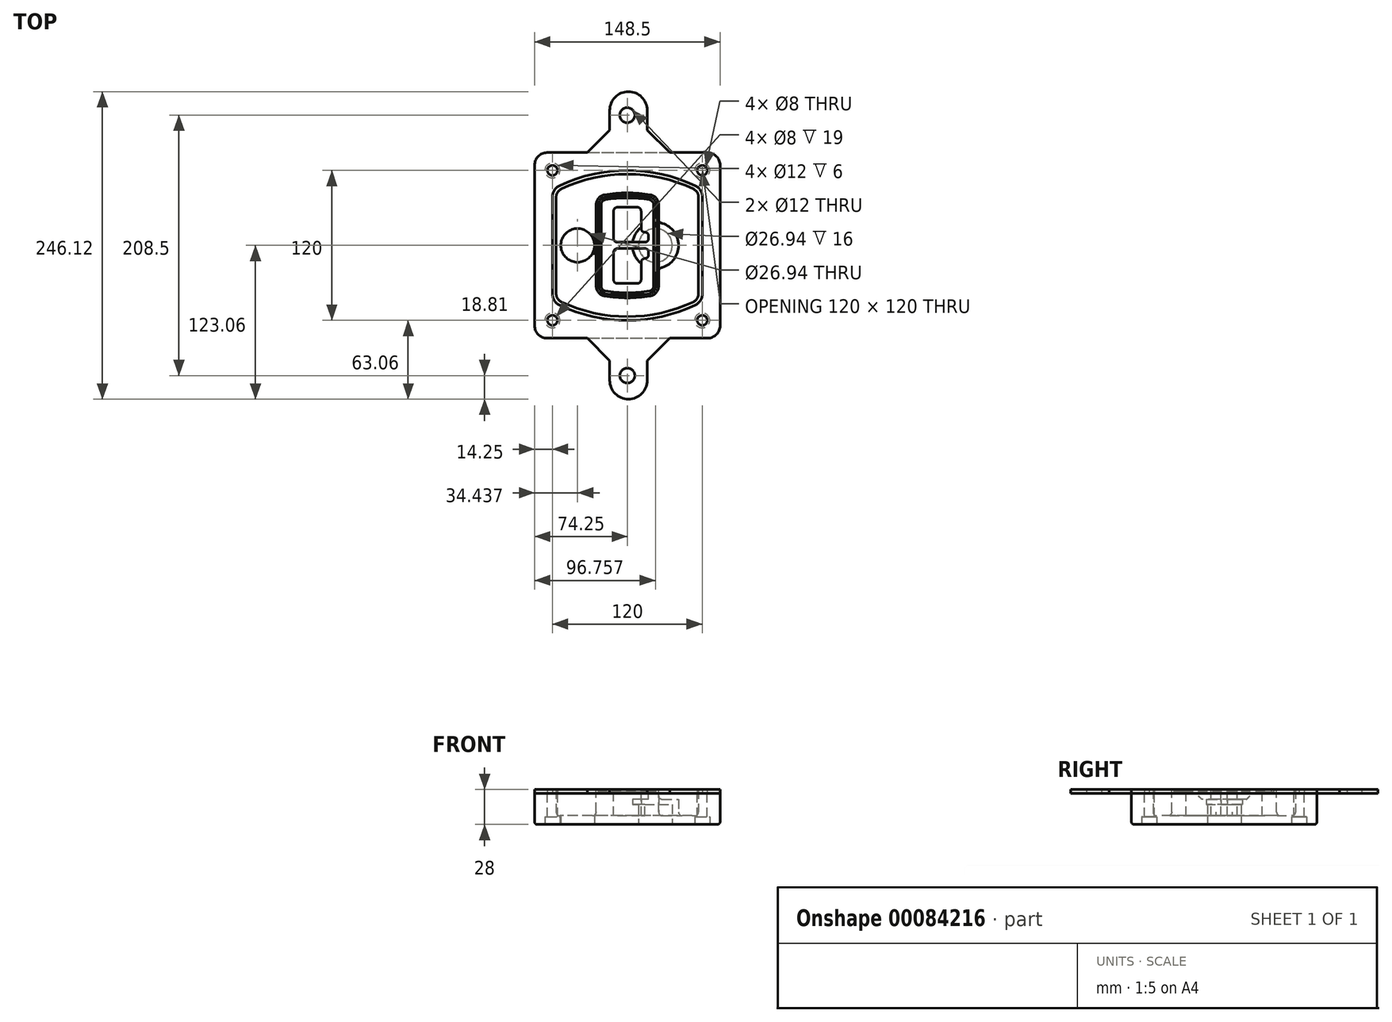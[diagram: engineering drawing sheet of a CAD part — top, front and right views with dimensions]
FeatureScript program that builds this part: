
annotation { "Feature Type Name" : "Feature", "Feature Type Description" : "" }
export const myFeature = defineFeature(function(context is Context, id is Id, definition is map)
    precondition{}
    {
        {
            var Q0;
            Q0=qCreatedBy(makeId("Top.planeOp"),FACE);
            var sketch = newSketch(context, id + "F0", { "sketchPlane" : qUnion([Q0])});
            skPoint(sketch, "E0.rect.middle", {"position": v(0, 0) * mm});
            skLineSegment(sketch, "E1.bottom", {"start": v(-64.25, -74.25) * mm, "end": v(64.25, -74.25) * mm});
            skLineSegment(sketch, "E1.top", {"start": v(-64.25, 74.25) * mm, "end": v(64.25, 74.25) * mm});
            skLineSegment(sketch, "E1.left", {"start": v(-74.25, -64.25) * mm, "end": v(-74.25, 64.25) * mm});
            skLineSegment(sketch, "E1.right", {"start": v(74.25, -64.25) * mm, "end": v(74.25, 64.25) * mm});
            skLineSegment(sketch, "E2", {"start": v(-74.25, 74.25) * mm, "end": v(74.25, -74.25) * mm, "construction": true});
            skLineSegment(sketch, "E3", {"start": v(74.25, 74.25) * mm, "end": v(-74.25, -74.25) * mm, "construction": true});
            skCircle(sketch, "E4", {"center": v(-60, 60) * mm, "radius": 4 * mm});
            skCircle(sketch, "E5", {"center": v(60, 60) * mm, "radius": 4 * mm});
            skCircle(sketch, "E6", {"center": v(60, -60) * mm, "radius": 4 * mm});
            skCircle(sketch, "E7", {"center": v(-60, -60) * mm, "radius": 4 * mm});
            skLineSegment(sketch, "E8", {"start": v(-60, 60) * mm, "end": v(60, 60) * mm, "construction": true});
            skLineSegment(sketch, "E9", {"start": v(60, 60) * mm, "end": v(60, -60) * mm, "construction": true});
            skLineSegment(sketch, "E10", {"start": v(60, -60) * mm, "end": v(-60, -60) * mm, "construction": true});
            skLineSegment(sketch, "E11", {"start": v(-60, -60) * mm, "end": v(-60, 60) * mm, "construction": true});
            skLineSegment(sketch, "E12", {"start": v(-60, 38.83) * mm, "end": v(-60, -38.83) * mm});
            skLineSegment(sketch, "E13", {"start": v(60, 38.83) * mm, "end": v(60, -38.83) * mm});
            skArc(sketch, "E14", {"start": v(54.26, 47.88) * mm, "mid": v(0, 60) * mm, "end": v(-54.26, 47.88) * mm});
            skArc(sketch, "E15", {"start": v(-54.26, -47.88) * mm, "mid": v(0, -60) * mm, "end": v(54.26, -47.88) * mm});
            skLineSegment(sketch, "E16", {"start": v(-60, 0) * mm, "end": v(60, 0) * mm, "construction": true});
            skPoint(sketch, "E17.visualSharp", {"position": v(-60, -45) * mm});
            skArc(sketch, "E17.filletArc", {"start": v(-60, -38.83) * mm, "mid": v(-58.44, -44.2) * mm, "end": v(-54.26, -47.88) * mm});
            skPoint(sketch, "E18.visualSharp", {"position": v(-60, 45) * mm});
            skArc(sketch, "E18.filletArc", {"start": v(-54.26, 47.88) * mm, "mid": v(-58.44, 44.2) * mm, "end": v(-60, 38.83) * mm});
            skPoint(sketch, "E19.visualSharp", {"position": v(60, 45) * mm});
            skArc(sketch, "E19.filletArc", {"start": v(60, 38.83) * mm, "mid": v(58.44, 44.2) * mm, "end": v(54.26, 47.88) * mm});
            skPoint(sketch, "E20.visualSharp", {"position": v(60, -45) * mm});
            skArc(sketch, "E20.filletArc", {"start": v(54.26, -47.88) * mm, "mid": v(58.44, -44.2) * mm, "end": v(60, -38.83) * mm});
            skPoint(sketch, "E21.visualSharp", {"position": v(-74.25, 74.25) * mm});
            skArc(sketch, "E21.filletArc", {"start": v(-64.25, 74.25) * mm, "mid": v(-71.32, 71.32) * mm, "end": v(-74.25, 64.25) * mm});
            skPoint(sketch, "E22.visualSharp", {"position": v(74.25, 74.25) * mm});
            skArc(sketch, "E22.filletArc", {"start": v(74.25, 64.25) * mm, "mid": v(71.32, 71.32) * mm, "end": v(64.25, 74.25) * mm});
            skPoint(sketch, "E23.visualSharp", {"position": v(74.25, -74.25) * mm});
            skArc(sketch, "E23.filletArc", {"start": v(64.25, -74.25) * mm, "mid": v(71.32, -71.32) * mm, "end": v(74.25, -64.25) * mm});
            skPoint(sketch, "E24.visualSharp", {"position": v(-74.25, -74.25) * mm});
            skArc(sketch, "E24.filletArc", {"start": v(-74.25, -64.25) * mm, "mid": v(-71.32, -71.32) * mm, "end": v(-64.25, -74.25) * mm});
            skArc(sketch, "E25.0", {"start": v(57, 38.83) * mm, "mid": v(55.9, 42.58) * mm, "end": v(52.98, 45.17) * mm});
            skLineSegment(sketch, "E25.1", {"start": v(57, 38.83) * mm, "end": v(57, -38.83) * mm});
            skArc(sketch, "E25.2", {"start": v(52.98, -45.17) * mm, "mid": v(55.9, -42.58) * mm, "end": v(57, -38.83) * mm});
            skArc(sketch, "E25.3", {"start": v(-52.98, -45.17) * mm, "mid": v(0, -57) * mm, "end": v(52.98, -45.17) * mm});
            skArc(sketch, "E25.4", {"start": v(-57, -38.83) * mm, "mid": v(-55.9, -42.58) * mm, "end": v(-52.98, -45.17) * mm});
            skArc(sketch, "E25.5", {"start": v(52.98, 45.17) * mm, "mid": v(0, 57) * mm, "end": v(-52.98, 45.17) * mm});
            skLineSegment(sketch, "E25.6", {"start": v(-57, 38.83) * mm, "end": v(-57, -38.83) * mm});
            skArc(sketch, "E25.7", {"start": v(-52.98, 45.17) * mm, "mid": v(-55.9, 42.58) * mm, "end": v(-57, 38.83) * mm});
            skArc(sketch, "E26.0", {"start": v(-55.96, 51.5) * mm, "mid": v(-61.82, 46.33) * mm, "end": v(-64, 38.83) * mm});
            skArc(sketch, "E26.1", {"start": v(55.96, 51.5) * mm, "mid": v(0, 64) * mm, "end": v(-55.96, 51.5) * mm});
            skArc(sketch, "E26.2", {"start": v(64, 38.83) * mm, "mid": v(61.82, 46.33) * mm, "end": v(55.96, 51.5) * mm});
            skLineSegment(sketch, "E26.3", {"start": v(64, 38.83) * mm, "end": v(64, -38.83) * mm});
            skArc(sketch, "E26.4", {"start": v(55.96, -51.5) * mm, "mid": v(61.82, -46.33) * mm, "end": v(64, -38.83) * mm});
            skLineSegment(sketch, "E26.5", {"start": v(-64, 38.83) * mm, "end": v(-64, -38.83) * mm});
            skArc(sketch, "E26.6", {"start": v(-55.96, -51.5) * mm, "mid": v(0, -64) * mm, "end": v(55.96, -51.5) * mm});
            skArc(sketch, "E26.7", {"start": v(-64, -38.83) * mm, "mid": v(-61.82, -46.33) * mm, "end": v(-55.96, -51.5) * mm});
            skSolve(sketch);
        }
        {
            var Q0;
            Q0=makeQuery(id+"F0.imprint","IMPRINT",FACE,{"disambiguationData":[TD([[makeQuery(id+"F0.imprint","IMPRINT",EDGE,{"derivedFrom":sQuery(id+"F0.wireOp",EDGE,"E1.bottom")}),1.0]])]});
            var Q1;
            Q1=makeQuery(id+"F0.imprint","IMPRINT",FACE,{"disambiguationData":[TD([[makeQuery(id+"F0.imprint","IMPRINT",EDGE,{"derivedFrom":sQuery(id+"F0.wireOp",EDGE,"E12")}),1.0]])]});
            var Q2;
            Q2=makeQuery(id+"F0.imprint","IMPRINT",FACE,{"disambiguationData":[TD([[makeQuery(id+"F0.imprint","IMPRINT",EDGE,{"derivedFrom":sQuery(id+"F0.wireOp",EDGE,"E25.0")}),1.0]])]});
            var Q3;
            Q3=makeQuery(id+"F0.imprint","IMPRINT",FACE,{"disambiguationData":[TD([[makeQuery(id+"F0.imprint","IMPRINT",EDGE,{"derivedFrom":sQuery(id+"F0.wireOp",EDGE,"E12")}),-1.0]])]});
            extrude(context, id + "F1", {"entities" : qUnion([Q0, Q1, Q2, Q3]), "oppositeDirection" : true, "depth" : 25 * mm});
        }
        {
            var Q0;
            Q0=makeQuery(id+"F0.imprint","IMPRINT",FACE,{"disambiguationData":[TD([[makeQuery(id+"F0.imprint","IMPRINT",EDGE,{"derivedFrom":sQuery(id+"F0.wireOp",EDGE,"E12")}),1.0]])]});
            extrude(context, id + "F2", {"entities" : qUnion([Q0]), "operationType" : NewBodyOperationType.ADD, "depth" : 3 * mm});
        }
        {
            var Q0;
            Q0=makeQuery(id+"F0.imprint","IMPRINT",FACE,{"disambiguationData":[TD([[makeQuery(id+"F0.imprint","IMPRINT",EDGE,{"derivedFrom":sQuery(id+"F0.wireOp",EDGE,"E25.0")}),1.0]])]});
            extrude(context, id + "F3", {"entities" : qUnion([Q0]), "operationType" : NewBodyOperationType.REMOVE, "oppositeDirection" : true, "depth" : 18 * mm});
        }
        {
            var Q0;
            Q0=makeQuery(id+"F2.opExtrude","CAP_FACE",FACE,{"disambiguationData":[OSD([sQuery(id+"F0.wireOp",EDGE,"E12"),sQuery(id+"F0.wireOp",EDGE,"E13"),sQuery(id+"F0.wireOp",EDGE,"E14"),sQuery(id+"F0.wireOp",EDGE,"E15"),sQuery(id+"F0.wireOp",EDGE,"E17.filletArc"),sQuery(id+"F0.wireOp",EDGE,"E18.filletArc"),sQuery(id+"F0.wireOp",EDGE,"E19.filletArc"),sQuery(id+"F0.wireOp",EDGE,"E20.filletArc"),sQuery(id+"F0.wireOp",EDGE,"E25.0"),sQuery(id+"F0.wireOp",EDGE,"E25.1"),sQuery(id+"F0.wireOp",EDGE,"E25.2"),sQuery(id+"F0.wireOp",EDGE,"E25.3"),sQuery(id+"F0.wireOp",EDGE,"E25.4"),sQuery(id+"F0.wireOp",EDGE,"E25.5"),sQuery(id+"F0.wireOp",EDGE,"E25.6"),sQuery(id+"F0.wireOp",EDGE,"E25.7")])],"isStart":false});
            var sketch = newSketch(context, id + "F4", { "sketchPlane" : qUnion([Q0])});
            skArc(sketch, "E27.0", {"start": v(-18.34, -40.45) * mm, "mid": v(0, -42) * mm, "end": v(18.34, -40.45) * mm});
            skArc(sketch, "E28.0", {"start": v(18.34, 40.45) * mm, "mid": v(0, 42) * mm, "end": v(-18.34, 40.45) * mm});
            skLineSegment(sketch, "E29", {"start": v(-25, 32.57) * mm, "end": v(-25, -32.57) * mm});
            skLineSegment(sketch, "E30", {"start": v(25, 32.57) * mm, "end": v(25, -32.57) * mm});
            skLineSegment(sketch, "E31", {"start": v(-25, 39.1) * mm, "end": v(25, 39.1) * mm, "construction": true});
            skLineSegment(sketch, "E32", {"start": v(-25, -39.1) * mm, "end": v(25, -39.1) * mm, "construction": true});
            skPoint(sketch, "E33.visualSharp", {"position": v(-25, 39.1) * mm});
            skArc(sketch, "E33.filletArc", {"start": v(-18.34, 40.45) * mm, "mid": v(-23.11, 37.73) * mm, "end": v(-25, 32.57) * mm});
            skPoint(sketch, "E34.visualSharp", {"position": v(25, 39.1) * mm});
            skArc(sketch, "E34.filletArc", {"start": v(25, 32.57) * mm, "mid": v(23.11, 37.73) * mm, "end": v(18.34, 40.45) * mm});
            skPoint(sketch, "E35.visualSharp", {"position": v(25, -39.1) * mm});
            skArc(sketch, "E35.filletArc", {"start": v(18.34, -40.45) * mm, "mid": v(23.11, -37.73) * mm, "end": v(25, -32.57) * mm});
            skPoint(sketch, "E36.visualSharp", {"position": v(-25, -39.1) * mm});
            skArc(sketch, "E36.filletArc", {"start": v(-25, -32.57) * mm, "mid": v(-23.11, -37.73) * mm, "end": v(-18.34, -40.45) * mm});
            skArc(sketch, "E37.0", {"start": v(52.98, 45.17) * mm, "mid": v(0, 57) * mm, "end": v(-52.98, 45.17) * mm});
            skArc(sketch, "E37.1", {"start": v(-52.98, 45.17) * mm, "mid": v(-55.9, 42.58) * mm, "end": v(-57, 38.83) * mm});
            skLineSegment(sketch, "E37.2", {"start": v(-57, 38.83) * mm, "end": v(-57, -38.83) * mm});
            skArc(sketch, "E37.3", {"start": v(-57, -38.83) * mm, "mid": v(-55.9, -42.58) * mm, "end": v(-52.98, -45.17) * mm});
            skArc(sketch, "E37.4", {"start": v(-52.98, -45.17) * mm, "mid": v(0, -57) * mm, "end": v(52.98, -45.17) * mm});
            skArc(sketch, "E37.5", {"start": v(52.98, -45.17) * mm, "mid": v(55.9, -42.58) * mm, "end": v(57, -38.83) * mm});
            skLineSegment(sketch, "E37.6", {"start": v(57, 38.83) * mm, "end": v(57, -38.83) * mm});
            skArc(sketch, "E37.7", {"start": v(57, 38.83) * mm, "mid": v(55.9, 42.58) * mm, "end": v(52.98, 45.17) * mm});
            skLineSegment(sketch, "E38.0", {"start": v(23, 32.57) * mm, "end": v(23, -32.57) * mm});
            skArc(sketch, "E38.1", {"start": v(18, -38.48) * mm, "mid": v(21.58, -36.44) * mm, "end": v(23, -32.57) * mm});
            skArc(sketch, "E38.2", {"start": v(-18, -38.48) * mm, "mid": v(0, -40) * mm, "end": v(18, -38.48) * mm});
            skArc(sketch, "E38.3", {"start": v(-23, -32.57) * mm, "mid": v(-21.58, -36.44) * mm, "end": v(-18, -38.48) * mm});
            skLineSegment(sketch, "E38.4", {"start": v(-23, 32.57) * mm, "end": v(-23, -32.57) * mm});
            skArc(sketch, "E38.5", {"start": v(23, 32.57) * mm, "mid": v(21.58, 36.44) * mm, "end": v(18, 38.48) * mm});
            skArc(sketch, "E38.6", {"start": v(-18, 38.48) * mm, "mid": v(-21.58, 36.44) * mm, "end": v(-23, 32.57) * mm});
            skArc(sketch, "E38.7", {"start": v(18, 38.48) * mm, "mid": v(0, 40) * mm, "end": v(-18, 38.48) * mm});
            skArc(sketch, "E39.0", {"start": v(21, 32.57) * mm, "mid": v(20.06, 35.15) * mm, "end": v(17.67, 36.5) * mm});
            skLineSegment(sketch, "E39.1", {"start": v(21, 32.57) * mm, "end": v(21, -32.57) * mm});
            skArc(sketch, "E39.2", {"start": v(17.67, -36.5) * mm, "mid": v(20.06, -35.15) * mm, "end": v(21, -32.57) * mm});
            skArc(sketch, "E39.3", {"start": v(-17.67, -36.5) * mm, "mid": v(0, -38) * mm, "end": v(17.67, -36.5) * mm});
            skArc(sketch, "E39.4", {"start": v(-21, -32.57) * mm, "mid": v(-20.06, -35.15) * mm, "end": v(-17.67, -36.5) * mm});
            skArc(sketch, "E39.5", {"start": v(17.67, 36.5) * mm, "mid": v(0, 38) * mm, "end": v(-17.67, 36.5) * mm});
            skLineSegment(sketch, "E39.6", {"start": v(-21, 32.57) * mm, "end": v(-21, -32.57) * mm});
            skArc(sketch, "E39.7", {"start": v(-17.67, 36.5) * mm, "mid": v(-20.06, 35.15) * mm, "end": v(-21, 32.57) * mm});
            skLineSegment(sketch, "E40", {"start": v(-25, 0) * mm, "end": v(25, 0) * mm, "construction": true});
            skLineSegment(sketch, "E41", {"start": v(-11, 5.5) * mm, "end": v(-11, 27.5) * mm});
            skLineSegment(sketch, "E42", {"start": v(-8, 30.5) * mm, "end": v(8, 30.5) * mm});
            skLineSegment(sketch, "E43", {"start": v(11, 27.5) * mm, "end": v(11, 13.5) * mm});
            skLineSegment(sketch, "E44", {"start": v(14, 10.5) * mm, "end": v(14, 10.5) * mm});
            skLineSegment(sketch, "E45", {"start": v(17, 7.5) * mm, "end": v(17, 5.5) * mm});
            skLineSegment(sketch, "E46", {"start": v(14, 2.5) * mm, "end": v(-8, 2.5) * mm});
            skPoint(sketch, "E47.visualSharp", {"position": v(-11, 30.5) * mm});
            skArc(sketch, "E47.filletArc", {"start": v(-8, 30.5) * mm, "mid": v(-10.12, 29.62) * mm, "end": v(-11, 27.5) * mm});
            skPoint(sketch, "E48.visualSharp", {"position": v(11, 30.5) * mm});
            skArc(sketch, "E48.filletArc", {"start": v(11, 27.5) * mm, "mid": v(10.12, 29.62) * mm, "end": v(8, 30.5) * mm});
            skPoint(sketch, "E49.visualSharp", {"position": v(11, 10.5) * mm});
            skArc(sketch, "E49.filletArc", {"start": v(11, 13.5) * mm, "mid": v(11.88, 11.38) * mm, "end": v(14, 10.5) * mm});
            skPoint(sketch, "E50.visualSharp", {"position": v(17, 10.5) * mm});
            skArc(sketch, "E50.filletArc", {"start": v(17, 7.5) * mm, "mid": v(16.12, 9.62) * mm, "end": v(14, 10.5) * mm});
            skPoint(sketch, "E51.visualSharp", {"position": v(17, 2.5) * mm});
            skArc(sketch, "E51.filletArc", {"start": v(14, 2.5) * mm, "mid": v(16.12, 3.38) * mm, "end": v(17, 5.5) * mm});
            skPoint(sketch, "E52.visualSharp", {"position": v(-11, 2.5) * mm});
            skArc(sketch, "E52.filletArc", {"start": v(-11, 5.5) * mm, "mid": v(-10.12, 3.38) * mm, "end": v(-8, 2.5) * mm});
            skLineSegment(sketch, "E53.0.MirrorCS", {"start": v(14, -2.5) * mm, "end": v(-8, -2.5) * mm});
            skArc(sketch, "E54.0.MirrorCS", {"start": v(-11, -5.5) * mm, "mid": v(-10.12, -3.38) * mm, "end": v(-8, -2.5) * mm});
            skLineSegment(sketch, "E55.0.MirrorCS", {"start": v(-11, -5.5) * mm, "end": v(-11, -27.5) * mm});
            skArc(sketch, "E56.0.MirrorCS", {"start": v(-8, -30.5) * mm, "mid": v(-10.12, -29.62) * mm, "end": v(-11, -27.5) * mm});
            skLineSegment(sketch, "E57.0.MirrorCS", {"start": v(-8, -30.5) * mm, "end": v(8, -30.5) * mm});
            skArc(sketch, "E58.0.MirrorCS", {"start": v(11, -27.5) * mm, "mid": v(10.12, -29.62) * mm, "end": v(8, -30.5) * mm});
            skLineSegment(sketch, "E59.0.MirrorCS", {"start": v(11, -27.5) * mm, "end": v(11, -13.5) * mm});
            skArc(sketch, "E60.0.MirrorCS", {"start": v(11, -13.5) * mm, "mid": v(11.88, -11.38) * mm, "end": v(14, -10.5) * mm});
            skArc(sketch, "E61.0.MirrorCS", {"start": v(17, -7.5) * mm, "mid": v(16.12, -9.62) * mm, "end": v(14, -10.5) * mm});
            skLineSegment(sketch, "E62.0.MirrorCS", {"start": v(17, -7.5) * mm, "end": v(17, -5.5) * mm});
            skArc(sketch, "E63.0.MirrorCS", {"start": v(14, -2.5) * mm, "mid": v(16.12, -3.38) * mm, "end": v(17, -5.5) * mm});
            skSolve(sketch);
        }
        {
            var Q0;
            Q0=makeQuery(id+"F4.imprint","IMPRINT",FACE,{"disambiguationData":[TD([[makeQuery(id+"F4.imprint","IMPRINT",EDGE,{"derivedFrom":sQuery(id+"F4.wireOp",EDGE,"E27.0")}),1.0]])]});
            var Q1;
            Q1=makeQuery(id+"F4.imprint","IMPRINT",FACE,{"disambiguationData":[TD([[makeQuery(id+"F4.imprint","IMPRINT",EDGE,{"derivedFrom":sQuery(id+"F4.wireOp",EDGE,"E38.0")}),-1.0]])]});
            var Q2;
            Q2=makeQuery(id+"F4.imprint","IMPRINT",FACE,{"disambiguationData":[TD([[makeQuery(id+"F4.imprint","IMPRINT",EDGE,{"derivedFrom":sQuery(id+"F4.wireOp",EDGE,"E39.0")}),1.0]])]});
            extrude(context, id + "F5", {"entities" : qUnion([Q0, Q1, Q2]), "operationType" : NewBodyOperationType.ADD, "endBound" : BoundingType.UP_TO_NEXT, "oppositeDirection" : true, "depth" : 25 * mm});
        }
        {
            var Q0;
            Q0=makeQuery(id+"F4.imprint","IMPRINT",FACE,{"disambiguationData":[TD([[makeQuery(id+"F4.imprint","IMPRINT",EDGE,{"derivedFrom":sQuery(id+"F4.wireOp",EDGE,"E38.0")}),-1.0]])]});
            extrude(context, id + "F6", {"entities" : qUnion([Q0]), "operationType" : NewBodyOperationType.REMOVE, "oppositeDirection" : true, "depth" : 2 * mm});
        }
        {
            var Q0;
            Q0=makeQuery(id+"F1.opExtrude","CAP_FACE",FACE,{"disambiguationData":[OSD([sQuery(id+"F0.wireOp",EDGE,"E1.bottom"),sQuery(id+"F0.wireOp",EDGE,"E1.top"),sQuery(id+"F0.wireOp",EDGE,"E1.left"),sQuery(id+"F0.wireOp",EDGE,"E1.right"),sQuery(id+"F0.wireOp",EDGE,"E4"),sQuery(id+"F0.wireOp",EDGE,"E5"),sQuery(id+"F0.wireOp",EDGE,"E6"),sQuery(id+"F0.wireOp",EDGE,"E7"),sQuery(id+"F0.wireOp",EDGE,"E21.filletArc"),sQuery(id+"F0.wireOp",EDGE,"E22.filletArc"),sQuery(id+"F0.wireOp",EDGE,"E23.filletArc"),sQuery(id+"F0.wireOp",EDGE,"E24.filletArc")])],"isStart":false});
            var sketch = newSketch(context, id + "F7", { "sketchPlane" : qUnion([Q0])});
            skCircle(sketch, "E64", {"center": v(22.5, 0) * mm, "radius": 13.47 * mm});
            skCircle(sketch, "E65", {"center": v(-39.81, 0) * mm, "radius": 13.47 * mm});
            skLineSegment(sketch, "E66", {"start": v(74.25, 0) * mm, "end": v(-74.25, 0) * mm});
            skCircle(sketch, "E67", {"center": v(22.5, 0) * mm, "radius": 18.47 * mm});
            skCircle(sketch, "E68", {"center": v(60, -60) * mm, "radius": 6 * mm});
            skCircle(sketch, "E69", {"center": v(-60, -60) * mm, "radius": 6 * mm});
            skCircle(sketch, "E70", {"center": v(-60, 60) * mm, "radius": 6 * mm});
            skCircle(sketch, "E71", {"center": v(60, 60) * mm, "radius": 6 * mm});
            skSolve(sketch);
        }
        {
            var Q0;
            {var subQ1=sQuery(id+"F7.wireOp",EDGE,"E66");var subQ4=sQuery(id+"F7.wireOp",EDGE,"E64");var subQ6=makeQuery(id+"F7.imprint","INTERSECT",VERTEX,{"disambiguationData":[OD(0.0)],"derivedFrom":[subQ4,subQ1]});Q0=makeQuery(id+"F7.imprint","IMPRINT",FACE,{"disambiguationData":[TD([[makeQuery(id+"F7.imprint","IMPRINT",EDGE,{"disambiguationData":[TD([[subQ6,-1.0]])],"derivedFrom":subQ4}),-1.0]])]});}
            var Q1;
            {var subQ0=sQuery(id+"F7.wireOp",EDGE,"E66");var subQ1=sQuery(id+"F7.wireOp",EDGE,"E64");var subQ3=makeQuery(id+"F7.imprint","INTERSECT",VERTEX,{"disambiguationData":[OD(0.0)],"derivedFrom":[subQ1,subQ0]});Q1=makeQuery(id+"F7.imprint","IMPRINT",FACE,{"disambiguationData":[TD([[makeQuery(id+"F7.imprint","IMPRINT",EDGE,{"disambiguationData":[TD([[subQ3,-1.0]])],"derivedFrom":subQ1}),1.0]])]});}
            var Q2;
            {var subQ0=sQuery(id+"F7.wireOp",EDGE,"E66");var subQ1=sQuery(id+"F7.wireOp",EDGE,"E64");var subQ3=makeQuery(id+"F7.imprint","INTERSECT",VERTEX,{"disambiguationData":[OD(0.0)],"derivedFrom":[subQ1,subQ0]});Q2=makeQuery(id+"F7.imprint","IMPRINT",FACE,{"disambiguationData":[TD([[makeQuery(id+"F7.imprint","IMPRINT",EDGE,{"disambiguationData":[TD([[subQ3,1.0]])],"derivedFrom":subQ1}),1.0]])]});}
            var Q3;
            {var subQ1=sQuery(id+"F7.wireOp",EDGE,"E66");var subQ4=sQuery(id+"F7.wireOp",EDGE,"E64");var subQ6=makeQuery(id+"F7.imprint","INTERSECT",VERTEX,{"disambiguationData":[OD(0.0)],"derivedFrom":[subQ4,subQ1]});Q3=makeQuery(id+"F7.imprint","IMPRINT",FACE,{"disambiguationData":[TD([[makeQuery(id+"F7.imprint","IMPRINT",EDGE,{"disambiguationData":[TD([[subQ6,1.0]])],"derivedFrom":subQ4}),-1.0]])]});}
            extrude(context, id + "F8", {"entities" : qUnion([Q0, Q1, Q2, Q3]), "operationType" : NewBodyOperationType.ADD, "oppositeDirection" : true, "depth" : 20 * mm});
        }
        {
            var Q0;
            {var subQ0=sQuery(id+"F7.wireOp",EDGE,"E66");var subQ1=sQuery(id+"F7.wireOp",EDGE,"E64");var subQ3=makeQuery(id+"F7.imprint","INTERSECT",VERTEX,{"disambiguationData":[OD(0.0)],"derivedFrom":[subQ1,subQ0]});Q0=makeQuery(id+"F7.imprint","IMPRINT",FACE,{"disambiguationData":[TD([[makeQuery(id+"F7.imprint","IMPRINT",EDGE,{"disambiguationData":[TD([[subQ3,-1.0]])],"derivedFrom":subQ1}),1.0]])]});}
            var Q1;
            {var subQ0=sQuery(id+"F7.wireOp",EDGE,"E66");var subQ1=sQuery(id+"F7.wireOp",EDGE,"E64");var subQ3=makeQuery(id+"F7.imprint","INTERSECT",VERTEX,{"disambiguationData":[OD(0.0)],"derivedFrom":[subQ1,subQ0]});Q1=makeQuery(id+"F7.imprint","IMPRINT",FACE,{"disambiguationData":[TD([[makeQuery(id+"F7.imprint","IMPRINT",EDGE,{"disambiguationData":[TD([[subQ3,1.0]])],"derivedFrom":subQ1}),1.0]])]});}
            extrude(context, id + "F9", {"entities" : qUnion([Q0, Q1]), "operationType" : NewBodyOperationType.REMOVE, "oppositeDirection" : true, "depth" : 16 * mm});
        }
        {
            var Q0;
            {var subQ0=sQuery(id+"F7.wireOp",EDGE,"E66");var subQ1=sQuery(id+"F7.wireOp",EDGE,"E65");var subQ3=makeQuery(id+"F7.imprint","INTERSECT",VERTEX,{"disambiguationData":[OD(0.0)],"derivedFrom":[subQ1,subQ0]});Q0=makeQuery(id+"F7.imprint","IMPRINT",FACE,{"disambiguationData":[TD([[makeQuery(id+"F7.imprint","IMPRINT",EDGE,{"disambiguationData":[TD([[subQ3,-1.0]])],"derivedFrom":subQ1}),1.0]])]});}
            var Q1;
            {var subQ0=sQuery(id+"F7.wireOp",EDGE,"E66");var subQ1=sQuery(id+"F7.wireOp",EDGE,"E65");var subQ3=makeQuery(id+"F7.imprint","INTERSECT",VERTEX,{"disambiguationData":[OD(0.0)],"derivedFrom":[subQ1,subQ0]});Q1=makeQuery(id+"F7.imprint","IMPRINT",FACE,{"disambiguationData":[TD([[makeQuery(id+"F7.imprint","IMPRINT",EDGE,{"disambiguationData":[TD([[subQ3,1.0]])],"derivedFrom":subQ1}),1.0]])]});}
            extrude(context, id + "F10", {"entities" : qUnion([Q0, Q1]), "operationType" : NewBodyOperationType.REMOVE, "oppositeDirection" : true, "depth" : 25 * mm});
        }
        {
            var Q0;
            Q0=makeQuery(id+"F7.imprint","IMPRINT",FACE,{"disambiguationData":[TD([[makeQuery(id+"F7.imprint","IMPRINT",EDGE,{"derivedFrom":sQuery(id+"F7.wireOp",EDGE,"E68")}),1.0]])]});
            var Q1;
            Q1=makeQuery(id+"F7.imprint","IMPRINT",FACE,{"disambiguationData":[TD([[makeQuery(id+"F7.imprint","IMPRINT",EDGE,{"derivedFrom":makeQuery(id+"F1.opExtrude","CAP_EDGE",EDGE,{"disambiguationData":[OSD([sQuery(id+"F0.wireOp",EDGE,"E5")])],"isStart":false})}),-1.0]])]});
            var Q2;
            Q2=makeQuery(id+"F7.imprint","IMPRINT",FACE,{"disambiguationData":[TD([[makeQuery(id+"F7.imprint","IMPRINT",EDGE,{"derivedFrom":sQuery(id+"F7.wireOp",EDGE,"E69")}),1.0]])]});
            var Q3;
            Q3=makeQuery(id+"F7.imprint","IMPRINT",FACE,{"disambiguationData":[TD([[makeQuery(id+"F7.imprint","IMPRINT",EDGE,{"derivedFrom":makeQuery(id+"F1.opExtrude","CAP_EDGE",EDGE,{"disambiguationData":[OSD([sQuery(id+"F0.wireOp",EDGE,"E4")])],"isStart":false})}),-1.0]])]});
            var Q4;
            Q4=makeQuery(id+"F7.imprint","IMPRINT",FACE,{"disambiguationData":[TD([[makeQuery(id+"F7.imprint","IMPRINT",EDGE,{"derivedFrom":sQuery(id+"F7.wireOp",EDGE,"E70")}),1.0]])]});
            var Q5;
            Q5=makeQuery(id+"F7.imprint","IMPRINT",FACE,{"disambiguationData":[TD([[makeQuery(id+"F7.imprint","IMPRINT",EDGE,{"derivedFrom":makeQuery(id+"F1.opExtrude","CAP_EDGE",EDGE,{"disambiguationData":[OSD([sQuery(id+"F0.wireOp",EDGE,"E7")])],"isStart":false})}),-1.0]])]});
            var Q6;
            Q6=makeQuery(id+"F7.imprint","IMPRINT",FACE,{"disambiguationData":[TD([[makeQuery(id+"F7.imprint","IMPRINT",EDGE,{"derivedFrom":sQuery(id+"F7.wireOp",EDGE,"E71")}),1.0]])]});
            var Q7;
            Q7=makeQuery(id+"F7.imprint","IMPRINT",FACE,{"disambiguationData":[TD([[makeQuery(id+"F7.imprint","IMPRINT",EDGE,{"derivedFrom":makeQuery(id+"F1.opExtrude","CAP_EDGE",EDGE,{"disambiguationData":[OSD([sQuery(id+"F0.wireOp",EDGE,"E6")])],"isStart":false})}),-1.0]])]});
            extrude(context, id + "F11", {"entities" : qUnion([Q0, Q1, Q2, Q3, Q4, Q5, Q6, Q7]), "operationType" : NewBodyOperationType.REMOVE, "oppositeDirection" : true, "depth" : 6 * mm});
        }
        {
            var Q0;
            Q0=makeQuery(id+"F9.boolean.opBoolean","COPY",FACE,{"derivedFrom":makeQuery(id+"F9.opExtrude","CAP_FACE",FACE,{"disambiguationData":[OSD([sQuery(id+"F7.wireOp",EDGE,"E64")])],"isStart":false})});
            var sketch = newSketch(context, id + "F12", { "sketchPlane" : qUnion([Q0])});
            skArc(sketch, "E72.0", {"start": v(11, 14.45) * mm, "mid": v(6.45, 9.13) * mm, "end": v(4.2, 2.5) * mm});
            skArc(sketch, "E72.1", {"start": v(4.2, -2.5) * mm, "mid": v(6.45, -9.13) * mm, "end": v(11, -14.45) * mm});
            skLineSegment(sketch, "E73", {"start": v(4.2, -2.5) * mm, "end": v(14, -2.5) * mm});
            skLineSegment(sketch, "E74.0", {"start": v(14, 2.5) * mm, "end": v(4.2, 2.5) * mm});
            skArc(sketch, "E74.1", {"start": v(14, 2.5) * mm, "mid": v(16.12, 3.38) * mm, "end": v(17, 5.5) * mm});
            skLineSegment(sketch, "E74.2", {"start": v(17, 7.5) * mm, "end": v(17, 5.5) * mm});
            skArc(sketch, "E74.3", {"start": v(17, 7.5) * mm, "mid": v(16.12, 9.62) * mm, "end": v(14, 10.5) * mm});
            skArc(sketch, "E74.4", {"start": v(11, 13.5) * mm, "mid": v(11.88, 11.38) * mm, "end": v(14, 10.5) * mm});
            skLineSegment(sketch, "E74.5", {"start": v(11, 14.45) * mm, "end": v(11, 13.5) * mm});
            skLineSegment(sketch, "E74.7", {"start": v(14, -2.5) * mm, "end": v(4.2, -2.5) * mm});
            skArc(sketch, "E74.8", {"start": v(14, -2.5) * mm, "mid": v(16.12, -3.38) * mm, "end": v(17, -5.5) * mm});
            skLineSegment(sketch, "E74.9", {"start": v(17, -7.5) * mm, "end": v(17, -5.5) * mm});
            skArc(sketch, "E74.10", {"start": v(17, -7.5) * mm, "mid": v(16.12, -9.62) * mm, "end": v(14, -10.5) * mm});
            skArc(sketch, "E74.11", {"start": v(11, -13.5) * mm, "mid": v(11.88, -11.38) * mm, "end": v(14, -10.5) * mm});
            skLineSegment(sketch, "E74.12", {"start": v(11, -14.45) * mm, "end": v(11, -13.5) * mm});
            skPoint(sketch, "E75.orphan", {"position": v(11, -27.5) * mm});
            skPoint(sketch, "E76.orphan", {"position": v(-8, -2.5) * mm});
            skPoint(sketch, "E77.orphan", {"position": v(-8, 2.5) * mm});
            skPoint(sketch, "E78.orphan", {"position": v(11, 27.5) * mm});
            skSolve(sketch);
        }
        {
            var Q0;
            {var subQ7=sQuery(id+"F12.wireOp",EDGE,"E72.0");var subQ14=sQuery(id+"F12.wireOp",EDGE,"E72.1");var subQ16=sQuery(id+"F12.wireOp",EDGE,"E74.1");var subQ18=sQuery(id+"F12.wireOp",EDGE,"E74.8");Q0=qUnion([makeQuery(id+"F12.imprint","IMPRINT",FACE,{"disambiguationData":[TD([[makeQuery(id+"F12.imprint","IMPRINT",EDGE,{"derivedFrom":subQ7}),1.0]])]}),makeQuery(id+"F12.imprint","IMPRINT",FACE,{"disambiguationData":[TD([[makeQuery(id+"F12.imprint","IMPRINT",EDGE,{"derivedFrom":subQ14}),1.0]])]}),makeQuery(id+"F12.imprint","IMPRINT",FACE,{"disambiguationData":[TD([[makeQuery(id+"F12.imprint","IMPRINT",EDGE,{"derivedFrom":subQ16}),1.0]])]}),makeQuery(id+"F12.imprint","IMPRINT",FACE,{"disambiguationData":[TD([[makeQuery(id+"F12.imprint","IMPRINT",EDGE,{"derivedFrom":subQ18}),-1.0]])]})]);}
            var Q1;
            Q1=makeQuery(id+"F5.boolean.opBoolean","SPLIT",FACE,{"disambiguationData":[TD([makeQuery(id+"F5.opExtrude","SWEPT_FACE",FACE,{"disambiguationData":[OSD([sQuery(id+"F4.wireOp",EDGE,"E41")])]})])],"derivedFrom":makeQuery(id+"F3.boolean.opBoolean","COPY",FACE,{"derivedFrom":makeQuery(id+"F3.opExtrude","CAP_FACE",FACE,{"disambiguationData":[OSD([sQuery(id+"F0.wireOp",EDGE,"E25.0"),sQuery(id+"F0.wireOp",EDGE,"E25.1"),sQuery(id+"F0.wireOp",EDGE,"E25.2"),sQuery(id+"F0.wireOp",EDGE,"E25.3"),sQuery(id+"F0.wireOp",EDGE,"E25.4"),sQuery(id+"F0.wireOp",EDGE,"E25.5"),sQuery(id+"F0.wireOp",EDGE,"E25.6"),sQuery(id+"F0.wireOp",EDGE,"E25.7")])],"isStart":false})})});
            extrude(context, id + "F13", {"entities" : qUnion([Q0]), "operationType" : NewBodyOperationType.REMOVE, "endBound" : BoundingType.UP_TO_SURFACE, "endBoundEntityFace" : qUnion([Q1]), "depth" : 25 * mm});
        }
        {
            var Q0;
            Q0=makeQuery(id+"F3.boolean.opBoolean","COPY",EDGE,{"derivedFrom":makeQuery(id+"F3.opExtrude","CAP_EDGE",EDGE,{"disambiguationData":[OSD([sQuery(id+"F0.wireOp",EDGE,"E25.6")])],"isStart":false})});
            var Q1;
            Q1=makeQuery(id+"F8.boolean.opBoolean","INTERSECT",EDGE,{"derivedFrom":[makeQuery(id+"F5.opExtrude","SWEPT_FACE",FACE,{"disambiguationData":[OSD([sQuery(id+"F4.wireOp",EDGE,"E30")])]}),makeQuery(id+"F8.opExtrude","CAP_FACE",FACE,{"disambiguationData":[OSD([sQuery(id+"F7.wireOp",EDGE,"E67")])],"isStart":false})]});
            var Q2;
            Q2=makeQuery(id+"F8.boolean.opBoolean","INTERSECT",EDGE,{"disambiguationData":[OD(1.0)],"derivedFrom":[makeQuery(id+"F5.opExtrude","SWEPT_FACE",FACE,{"disambiguationData":[OSD([sQuery(id+"F4.wireOp",EDGE,"E30")])]}),makeQuery(id+"F8.opExtrude","SWEPT_FACE",FACE,{"disambiguationData":[OSD([sQuery(id+"F7.wireOp",EDGE,"E67")])]})]});
            var Q3;
            {var subQ0=sQuery(id+"F4.wireOp",EDGE,"E30");Q3=makeQuery(id+"F8.boolean.opBoolean","SPLIT",EDGE,{"disambiguationData":[TD([makeQuery(id+"F5.opExtrude","SWEPT_FACE",FACE,{"disambiguationData":[OSD([sQuery(id+"F4.wireOp",EDGE,"E35.filletArc")])]})])],"derivedFrom":makeQuery(id+"F5.opExtrude","CAP_EDGE",EDGE,{"disambiguationData":[OSD([subQ0])],"isStart":false})});}
            var Q4;
            {var subQ0=sQuery(id+"F0.wireOp",EDGE,"E25.7");var subQ1=sQuery(id+"F0.wireOp",EDGE,"E25.1");var subQ2=sQuery(id+"F0.wireOp",EDGE,"E25.6");var subQ3=sQuery(id+"F0.wireOp",EDGE,"E25.5");var subQ4=sQuery(id+"F0.wireOp",EDGE,"E25.4");var subQ5=sQuery(id+"F0.wireOp",EDGE,"E25.0");var subQ6=sQuery(id+"F0.wireOp",EDGE,"E25.2");var subQ7=sQuery(id+"F0.wireOp",EDGE,"E25.3");Q4=makeQuery(id+"F8.boolean.opBoolean","INTERSECT",EDGE,{"derivedFrom":[makeQuery(id+"F5.boolean.opBoolean","SPLIT",FACE,{"disambiguationData":[TD([makeQuery(id+"F2.opExtrude","SWEPT_FACE",FACE,{"disambiguationData":[OSD([subQ5])]})])],"derivedFrom":makeQuery(id+"F3.boolean.opBoolean","COPY",FACE,{"derivedFrom":makeQuery(id+"F3.opExtrude","CAP_FACE",FACE,{"disambiguationData":[OSD([subQ5,subQ1,subQ6,subQ7,subQ4,subQ3,subQ2,subQ0])],"isStart":false})})}),makeQuery(id+"F8.opExtrude","SWEPT_FACE",FACE,{"disambiguationData":[OSD([sQuery(id+"F7.wireOp",EDGE,"E67")])]})]});}
            var Q5;
            Q5=makeQuery(id+"F8.boolean.opBoolean","INTERSECT",EDGE,{"disambiguationData":[OD(0.0)],"derivedFrom":[makeQuery(id+"F5.opExtrude","SWEPT_FACE",FACE,{"disambiguationData":[OSD([sQuery(id+"F4.wireOp",EDGE,"E30")])]}),makeQuery(id+"F8.opExtrude","SWEPT_FACE",FACE,{"disambiguationData":[OSD([sQuery(id+"F7.wireOp",EDGE,"E67")])]})]});
            fillet(context, id + "F14", {"entities" : qUnion([Q0, Q1, Q2, Q3, Q4, Q5]), "radius" : 3 * mm, "tangentPropagation" : true, "allowEdgeOverflow" : false});
        }
        {
            var Q0;
            Q0=makeQuery(id+"F1.opExtrude","CAP_EDGE",EDGE,{"disambiguationData":[OSD([sQuery(id+"F0.wireOp",EDGE,"E1.bottom")])],"isStart":false});
            fillet(context, id + "F15", {"entities" : qUnion([Q0]), "radius" : 2 * mm, "tangentPropagation" : true, "allowEdgeOverflow" : false});
        }
        {
            var Q0;
            {var subQ0=sQuery(id+"F0.wireOp",EDGE,"E22.filletArc");var subQ1=sQuery(id+"F0.wireOp",EDGE,"E7");var subQ2=sQuery(id+"F0.wireOp",EDGE,"E6");var subQ3=sQuery(id+"F0.wireOp",EDGE,"E5");var subQ4=sQuery(id+"F0.wireOp",EDGE,"E4");var subQ5=sQuery(id+"F0.wireOp",EDGE,"E1.bottom");var subQ6=sQuery(id+"F0.wireOp",EDGE,"E21.filletArc");var subQ7=sQuery(id+"F0.wireOp",EDGE,"E1.top");var subQ8=sQuery(id+"F0.wireOp",EDGE,"E1.left");var subQ9=sQuery(id+"F0.wireOp",EDGE,"E1.right");var subQ10=sQuery(id+"F0.wireOp",EDGE,"E23.filletArc");var subQ11=sQuery(id+"F0.wireOp",EDGE,"E24.filletArc");Q0=makeQuery(id+"F2.boolean.opBoolean","SPLIT",FACE,{"disambiguationData":[TD([makeQuery(id+"F1.opExtrude","SWEPT_FACE",FACE,{"disambiguationData":[OSD([subQ5])]})])],"derivedFrom":makeQuery(id+"F1.opExtrude","CAP_FACE",FACE,{"disambiguationData":[OSD([subQ5,subQ7,subQ8,subQ9,subQ4,subQ3,subQ2,subQ1,subQ6,subQ0,subQ10,subQ11])],"isStart":true})});}
            var sketch = newSketch(context, id + "F16", { "sketchPlane" : qUnion([Q0])});
            skLineSegment(sketch, "E79", {"start": v(0, 74.25) * mm, "end": v(0, 104.25) * mm, "construction": true});
            skCircle(sketch, "E80", {"center": v(0, 104.25) * mm, "radius": 6 * mm});
            skArc(sketch, "E81", {"start": v(15.88, 108.06) * mm, "mid": v(0.88, 123.06) * mm, "end": v(-14.12, 108.06) * mm});
            skLineSegment(sketch, "E82", {"start": v(-14.12, 108.06) * mm, "end": v(-14.12, 92.25) * mm});
            skLineSegment(sketch, "E83", {"start": v(15.88, 108.06) * mm, "end": v(15.88, 92.25) * mm});
            skLineSegment(sketch, "E84", {"start": v(15.88, 92.25) * mm, "end": v(33.88, 74.25) * mm});
            skLineSegment(sketch, "E85", {"start": v(-14.12, 92.25) * mm, "end": v(-32.12, 74.25) * mm});
            skLineSegment(sketch, "E86", {"start": v(-74.25, 0) * mm, "end": v(74.25, 0) * mm, "construction": true});
            skLineSegment(sketch, "E87.MirrorCS", {"start": v(15.88, -92.25) * mm, "end": v(33.88, -74.25) * mm});
            skLineSegment(sketch, "E88.MirrorCS", {"start": v(15.88, -108.06) * mm, "end": v(15.88, -92.25) * mm});
            skArc(sketch, "E89.MirrorCS", {"start": v(15.88, -108.06) * mm, "mid": v(0.88, -123.06) * mm, "end": v(-14.12, -108.06) * mm});
            skLineSegment(sketch, "E90.MirrorCS", {"start": v(-14.12, -108.06) * mm, "end": v(-14.12, -92.25) * mm});
            skLineSegment(sketch, "E91.MirrorCS", {"start": v(-14.12, -92.25) * mm, "end": v(-32.12, -74.25) * mm});
            skLineSegment(sketch, "E92.MirrorCS", {"start": v(0, -74.25) * mm, "end": v(0, -104.25) * mm, "construction": true});
            skCircle(sketch, "E93.MirrorC", {"center": v(0, -104.25) * mm, "radius": 6 * mm});
            skSolve(sketch);
        }
        {
            var Q0;
            {var subQ0=sQuery(id+"F16.wireOp",EDGE,"E87.MirrorCS");Q0=makeQuery(id+"F16.imprint","IMPRINT",FACE,{"disambiguationData":[TD([[makeQuery(id+"F16.imprint","IMPRINT",EDGE,{"derivedFrom":subQ0}),1.0]])]});}
            var Q1;
            Q1=makeQuery(id+"F16.imprint","IMPRINT",FACE,{"disambiguationData":[TD([[makeQuery(id+"F16.imprint","IMPRINT",EDGE,{"derivedFrom":sQuery(id+"F16.wireOp",EDGE,"E80")}),-1.0]])]});
            var Q2;
            Q2=makeQuery(id+"F16.imprint","IMPRINT",FACE,{"disambiguationData":[TD([[makeQuery(id+"F16.imprint","IMPRINT",EDGE,{"derivedFrom":makeQuery(id+"F1.opExtrude","CAP_EDGE",EDGE,{"disambiguationData":[OSD([sQuery(id+"F0.wireOp",EDGE,"E1.left")])],"isStart":true})}),-1.0]])]});
            var Q3;
            Q3=makeQuery(id+"F2.opExtrude","CAP_FACE",FACE,{"disambiguationData":[OSD([sQuery(id+"F0.wireOp",EDGE,"E12"),sQuery(id+"F0.wireOp",EDGE,"E13"),sQuery(id+"F0.wireOp",EDGE,"E14"),sQuery(id+"F0.wireOp",EDGE,"E15"),sQuery(id+"F0.wireOp",EDGE,"E17.filletArc"),sQuery(id+"F0.wireOp",EDGE,"E18.filletArc"),sQuery(id+"F0.wireOp",EDGE,"E19.filletArc"),sQuery(id+"F0.wireOp",EDGE,"E20.filletArc"),sQuery(id+"F0.wireOp",EDGE,"E25.0"),sQuery(id+"F0.wireOp",EDGE,"E25.1"),sQuery(id+"F0.wireOp",EDGE,"E25.2"),sQuery(id+"F0.wireOp",EDGE,"E25.3"),sQuery(id+"F0.wireOp",EDGE,"E25.4"),sQuery(id+"F0.wireOp",EDGE,"E25.5"),sQuery(id+"F0.wireOp",EDGE,"E25.6"),sQuery(id+"F0.wireOp",EDGE,"E25.7")])],"isStart":false});
            var Q4;
            Q4=makeQuery(id+"F1.opExtrude","SWEPT_BODY",BODY,{"disambiguationData":[OSD([sQuery(id+"F0.wireOp",EDGE,"E1.bottom"),sQuery(id+"F0.wireOp",EDGE,"E1.top"),sQuery(id+"F0.wireOp",EDGE,"E1.left"),sQuery(id+"F0.wireOp",EDGE,"E1.right"),sQuery(id+"F0.wireOp",EDGE,"E4"),sQuery(id+"F0.wireOp",EDGE,"E5"),sQuery(id+"F0.wireOp",EDGE,"E6"),sQuery(id+"F0.wireOp",EDGE,"E7"),sQuery(id+"F0.wireOp",EDGE,"E21.filletArc"),sQuery(id+"F0.wireOp",EDGE,"E22.filletArc"),sQuery(id+"F0.wireOp",EDGE,"E23.filletArc"),sQuery(id+"F0.wireOp",EDGE,"E24.filletArc")])]});
            extrude(context, id + "F17", {"entities" : qUnion([Q0, Q1, Q2]), "endBound" : BoundingType.UP_TO_SURFACE, "endBoundEntityFace" : qUnion([Q3]), "endBoundEntityBody" : qUnion([Q4]), "depth" : 25 * mm});
        }
    });
